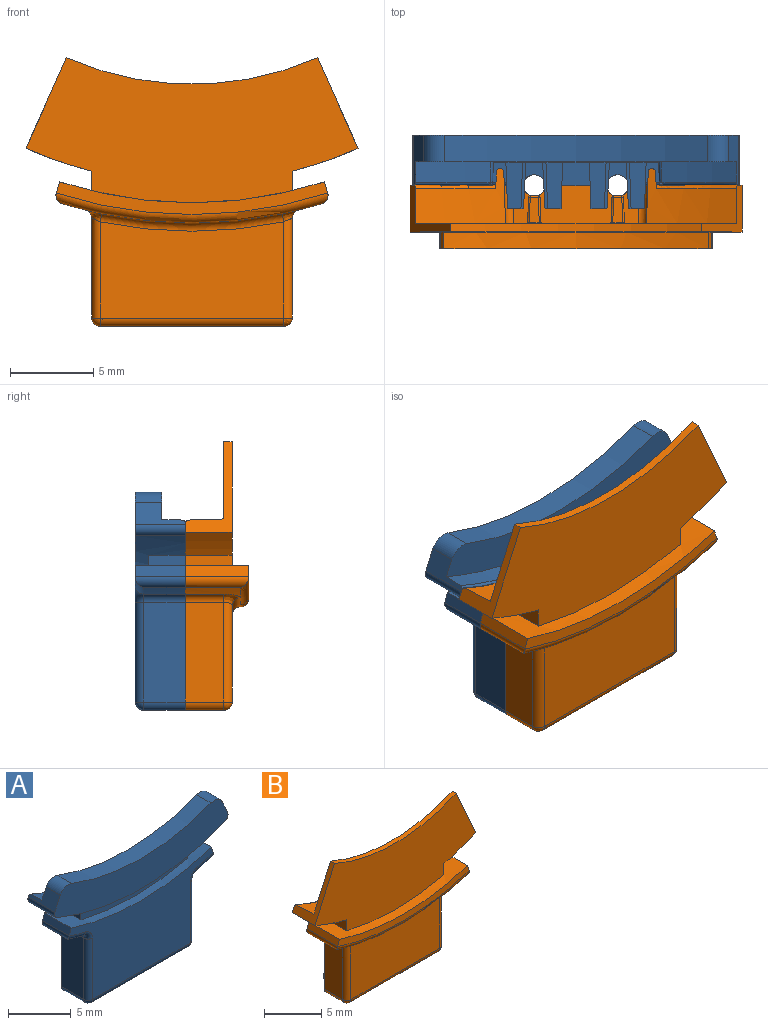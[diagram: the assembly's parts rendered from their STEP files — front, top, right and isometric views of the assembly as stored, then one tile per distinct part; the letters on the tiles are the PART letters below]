
ASSEMBLY  parts=2 mates=1
PART A: 159 faces, bbox 19.8x4.6x13.2 mm
  f0: cylinder r=0.47mm len=1.8mm, axis (0,1,0), area 5.4mm2, adj f12,f54
  f1: cylinder r=0.47mm len=1.8mm, axis (0,1,0), area 5.4mm2, adj f9,f53
  f2: cylinder r=25.6mm len=15.82mm, axis (0,-1,0), area 21.6mm2, adj f9,f12,f17,f21,f22,f26,f27,f31
  f3: cylinder r=24.45mm len=18.95mm, axis (0,-1,0), area 31.7mm2, adj f9,f12,f18,f22,f23,f25,f26,f31
  f4: cylinder r=21.5mm len=15.73mm, axis (0,-1,0), area 25.8mm2, adj f5,f14,f15,f18
  f5: plane 19.2x12.01mm, normal (0,1,0), area 97.3mm2, adj f4,f6,f7,f10,f11,f13,f14,f15
  f6: plane 1.68x1.59mm, normal (0,0.03,1), area 1.4mm2, adj f5,f8,f9,f37,f104,f144
  f7: plane 1.7x1.4mm, normal (0,0.03,1), area 2.3mm2, adj f5,f8,f99,f145
  f8: plane 3.7x1mm, normal (0,1,0), area 3.6mm2, adj f6,f7,f11,f30,f36,f37,f78,f79
  f9: plane 11.24x6.65mm, normal (0,1,0), area 15.3mm2, adj f1,f2,f3,f6,f16,f25,f26,f27
  f10: plane 1.21x0.84mm, normal (0,0.03,1), area 1mm2, adj f5,f35,f102,f153
  f11: plane 1.68x1.59mm, normal (0,0.03,1), area 1.4mm2, adj f5,f8,f12,f36,f57,f79
  f12: plane 11.24x6.65mm, normal (0,1,0), area 15.3mm2, adj f0,f2,f3,f11,f19,f20,f21,f22
  f13: plane 1.21x0.84mm, normal (0,0.03,1), area 1mm2, adj f5,f34,f56,f158
  f14: cylinder r=1mm len=1.6mm, axis (0,-1,0), area 2.4mm2, adj f4,f5,f18,f24
  f15: cylinder r=1mm len=1.6mm, axis (0,-1,0), area 2.4mm2, adj f4,f5,f16,f18
  f16: plane 3x1.34mm, normal (0.91,0,0.41), area 2.8mm2, adj f5,f9,f15,f18,f25,f33,f149
  f17: plane 16.25x8.15mm, normal (0,-1,0), area 82mm2, adj f2,f21,f27,f38,f40,f41,f43,f46
  f18: plane 19.57x4.51mm, normal (0,-1,0), area 56.3mm2, adj f3,f4,f14,f15,f16,f23,f24,f25
  f19: plane 5.99x2.5mm, normal (-1,0,0), area 15mm2, adj f12,f39,f42,f43
  f20: cylinder r=26.8mm len=2.5mm, axis (0,-1,0), area 3.7mm2, adj f12,f38,f39,f40
  f21: plane 3x0.66mm, normal (-0.95,0,0.31), area 2.1mm2, adj f2,f12,f17,f38
  f22: plane 2.2x1.18mm, normal (-1,0,0), area 2.6mm2, adj f2,f3,f12,f31
  f23: cylinder r=0.5mm len=3mm, axis (0,-1,0), area 2.4mm2, adj f3,f12,f18,f24
  f24: plane 3x1.34mm, normal (-0.91,0,0.41), area 2.8mm2, adj f5,f12,f14,f18,f23,f32,f155
  f25: cylinder r=0.5mm len=3mm, axis (0,-1,0), area 2.4mm2, adj f3,f9,f16,f18
  f26: plane 2.2x1.18mm, normal (1,0,0), area 2.6mm2, adj f2,f3,f9,f31
  f27: plane 3x0.66mm, normal (0.95,0,0.31), area 2.1mm2, adj f2,f9,f17,f50
  f28: cylinder r=26.8mm len=2.5mm, axis (0,-1,0), area 3.7mm2, adj f9,f48,f50,f52
  f29: plane 5.99x2.5mm, normal (1,0,0), area 15mm2, adj f9,f45,f48,f49
  f30: plane 11x2.5mm, normal (0,0,-1), area 26.2mm2, adj f8,f9,f12,f36,f37,f42,f45,f46
  f31: plane 12x1.9mm, normal (0,-1,0), area 13.9mm2, adj f2,f3,f22,f26
  f32: cone r=23.65mm half-angle=2deg, axis (0,1,0), area 5.7mm2, adj f5,f24,f154,f155
  f33: cone r=23.65mm half-angle=2deg, axis (0,1,0), area 5.7mm2, adj f5,f16,f149,f150
  f34: plane 7.56x1.21mm, normal (1,0.03,0), area 9.1mm2, adj f5,f13,f154,f157
  f35: plane 7.56x1.21mm, normal (-1,0.03,0), area 9.1mm2, adj f5,f10,f150,f152
  f36: cylinder r=0.65mm len=1.3mm, axis (0,0,-1), area 2mm2, adj f8,f11,f12,f30
  f37: cylinder r=0.65mm len=1.3mm, axis (0,0,-1), area 2mm2, adj f6,f8,f9,f30
  f38: cylinder r=0.5mm len=3mm, axis (0,-1,0), area 2.2mm2, adj f12,f17,f20,f21,f40
  f39: cylinder r=0.5mm len=2.5mm, axis (0,-1,0), area 1.7mm2, adj f12,f19,f20,f41
  f40: torus R=26.3mm, axis (0,-1,0), area 1.3mm2, adj f17,f20,f38,f41
  f41: torus R=1mm, axis (0,-1,0), area 0.7mm2, adj f17,f39,f40,f43
  f42: cylinder r=0.5mm len=2.5mm, axis (0,-1,0), area 2mm2, adj f12,f19,f30,f44
  f43: cylinder r=0.5mm len=5.99mm, axis (0,0,-1), area 4.7mm2, adj f17,f19,f41,f44
  f44: sphere r=0.5mm, area 0.5mm2, adj f42,f43,f46
  f45: cylinder r=0.5mm len=2.5mm, axis (0,-1,0), area 2mm2, adj f9,f29,f30,f47
  f46: cylinder r=0.5mm len=11mm, axis (1,0,0), area 8.6mm2, adj f17,f30,f44,f47
  f47: sphere r=0.5mm, area 0.2mm2, adj f45,f46,f49
  f48: cylinder r=0.5mm len=2.5mm, axis (0,-1,0), area 1.7mm2, adj f9,f28,f29,f51
  f49: cylinder r=0.5mm len=5.99mm, axis (0,0,1), area 4.7mm2, adj f17,f29,f47,f51
  f50: cylinder r=0.5mm len=3mm, axis (0,-1,0), area 2.2mm2, adj f9,f17,f27,f28,f52
  f51: torus R=1mm, axis (0,-1,0), area 0.7mm2, adj f17,f48,f49,f52
  f52: torus R=26.3mm, axis (0,-1,0), area 1.3mm2, adj f17,f28,f50,f51
  f53: plane 0.95x0.95mm, normal (0,1,0), area 0.7mm2, adj f1
  f54: plane 0.95x0.95mm, normal (0,1,0), area 0.7mm2, adj f0
  f55: plane 1.4x0.4mm, normal (0,0.03,-1), area 0.5mm2, adj f12,f57,f77,f148
  f56: plane 5.46x2.81mm, normal (-1,0.03,0), area 14mm2, adj f5,f12,f13,f58,f77,f148,f158
  f57: plane 2.8x0.47mm, normal (1,0.03,0), area 1.2mm2, adj f5,f11,f12,f55,f76,f77
  f58: plane 2.8x1mm, normal (0,0.03,1), area 2.5mm2, adj f5,f56,f59,f77
  f59: plane 2.8x0.6mm, normal (1,0.03,0), area 1.4mm2, adj f5,f58,f60,f77
  f60: plane 2.8x0.3mm, normal (0,0.03,1), area 0.5mm2, adj f5,f59,f61,f77
  f61: plane 2.8x0.5mm, normal (0.93,0.03,-0.37), area 1.3mm2, adj f5,f60,f62,f77
  f62: plane 2.8x0.52mm, normal (1,0.03,0), area 1.3mm2, adj f5,f61,f63,f77
  f63: plane 2.8x0.3mm, normal (0,0.03,1), area 0.5mm2, adj f5,f62,f64,f77
  f64: plane 2.8x0.5mm, normal (0.93,0.03,-0.37), area 1.3mm2, adj f5,f63,f65,f77
  f65: plane 2.8x0.52mm, normal (1,0.03,0), area 1.3mm2, adj f5,f64,f66,f77
  f66: plane 2.8x0.3mm, normal (0,0.03,1), area 0.5mm2, adj f5,f65,f67,f77
  f67: plane 2.8x0.5mm, normal (0.93,0.03,-0.37), area 1.3mm2, adj f5,f66,f68,f77
  f68: plane 2.8x0.52mm, normal (1,0.03,0), area 1.3mm2, adj f5,f67,f69,f77
  f69: plane 2.8x0.3mm, normal (0,0.03,1), area 0.5mm2, adj f5,f68,f70,f77
  f70: plane 2.8x0.5mm, normal (0.93,0.03,-0.37), area 1.3mm2, adj f5,f69,f71,f77
  f71: plane 2.8x0.52mm, normal (1,0.03,0), area 1.3mm2, adj f5,f70,f72,f77
  f72: plane 2.8x0.3mm, normal (0,0.03,1), area 0.5mm2, adj f5,f71,f73,f77
  f73: plane 2.8x0.5mm, normal (0.93,0.03,-0.37), area 1.3mm2, adj f5,f72,f74,f77
  f74: plane 2.8x0.52mm, normal (1,0.03,0), area 1.3mm2, adj f5,f73,f75,f77
  f75: plane 2.8x0.3mm, normal (0,0.03,1), area 0.5mm2, adj f5,f74,f76,f77
  f76: plane 2.8x0.5mm, normal (0.93,0.03,-0.37), area 1.3mm2, adj f5,f57,f75,f77
  f77: plane 5.82x0.98mm, normal (0,1,0), area 4.8mm2, adj f55,f56,f57,f58,f59,f60,f61,f62
  f78: plane 1.4x0.9mm, normal (0,0.03,-1), area 1.2mm2, adj f8,f79,f99,f100
  f79: plane 2.8x0.47mm, normal (-1,0.03,0), area 1.2mm2, adj f5,f8,f11,f78,f80,f100
  f80: plane 2.8x0.5mm, normal (-0.93,0.03,-0.37), area 1.3mm2, adj f5,f79,f81,f100
  f81: plane 2.8x0.3mm, normal (0,0.03,1), area 0.5mm2, adj f5,f80,f82,f100
  f82: plane 2.8x0.52mm, normal (-1,0.03,0), area 1.3mm2, adj f5,f81,f83,f100
  f83: plane 2.8x0.5mm, normal (-0.93,0.03,-0.37), area 1.3mm2, adj f5,f82,f84,f100
  f84: plane 2.8x0.3mm, normal (0,0.03,1), area 0.5mm2, adj f5,f83,f85,f100
  f85: plane 2.8x0.52mm, normal (-1,0.03,0), area 1.3mm2, adj f5,f84,f86,f100
  f86: plane 2.8x0.5mm, normal (-0.93,0.03,-0.37), area 1.3mm2, adj f5,f85,f87,f100
  f87: plane 2.8x0.3mm, normal (0,0.03,1), area 0.5mm2, adj f5,f86,f88,f100
  f88: plane 2.8x0.52mm, normal (-1,0.03,0), area 1.3mm2, adj f5,f87,f89,f100
  f89: plane 2.8x0.5mm, normal (-0.93,0.03,-0.37), area 1.3mm2, adj f5,f88,f90,f100
  f90: plane 2.8x0.3mm, normal (0,0.03,1), area 0.5mm2, adj f5,f89,f91,f100
  f91: plane 2.8x0.52mm, normal (-1,0.03,0), area 1.3mm2, adj f5,f90,f92,f100
  f92: plane 2.8x0.5mm, normal (-0.93,0.03,-0.37), area 1.3mm2, adj f5,f91,f93,f100
  f93: plane 2.8x0.3mm, normal (0,0.03,1), area 0.5mm2, adj f5,f92,f94,f100
  f94: plane 2.8x0.52mm, normal (-1,0.03,0), area 1.3mm2, adj f5,f93,f95,f100
  f95: plane 2.8x0.5mm, normal (-0.93,0.03,-0.37), area 1.3mm2, adj f5,f94,f96,f100
  f96: plane 2.8x0.3mm, normal (0,0.03,1), area 0.5mm2, adj f5,f95,f97,f100
  f97: plane 2.8x0.6mm, normal (-1,0.03,0), area 1.4mm2, adj f5,f96,f98,f100
  f98: plane 2.8x1mm, normal (0,0.03,1), area 2.5mm2, adj f5,f97,f99,f100
  f99: plane 5.95x2.8mm, normal (1,0.03,0), area 16.4mm2, adj f5,f7,f8,f78,f98,f100
  f100: plane 5.8x0.96mm, normal (0,1,0), area 4.8mm2, adj f78,f79,f80,f81,f82,f83,f84,f85
  f101: plane 1.4x0.4mm, normal (0,0.03,-1), area 0.5mm2, adj f9,f104,f123,f147
  f102: plane 5.46x2.81mm, normal (1,0.03,0), area 14mm2, adj f5,f9,f10,f103,f123,f147,f153
  f103: plane 2.8x1mm, normal (0,0.03,1), area 2.5mm2, adj f5,f102,f122,f123
  f104: plane 2.8x0.47mm, normal (-1,0.03,0), area 1.2mm2, adj f5,f6,f9,f101,f105,f123
  f105: plane 2.8x0.5mm, normal (-0.93,0.03,-0.37), area 1.3mm2, adj f5,f104,f106,f123
  f106: plane 2.8x0.3mm, normal (0,0.03,1), area 0.5mm2, adj f5,f105,f107,f123
  f107: plane 2.8x0.52mm, normal (-1,0.03,0), area 1.3mm2, adj f5,f106,f108,f123
  f108: plane 2.8x0.5mm, normal (-0.93,0.03,-0.37), area 1.3mm2, adj f5,f107,f109,f123
  f109: plane 2.8x0.3mm, normal (0,0.03,1), area 0.5mm2, adj f5,f108,f110,f123
  f110: plane 2.8x0.52mm, normal (-1,0.03,0), area 1.3mm2, adj f5,f109,f111,f123
  f111: plane 2.8x0.5mm, normal (-0.93,0.03,-0.37), area 1.3mm2, adj f5,f110,f112,f123
  f112: plane 2.8x0.3mm, normal (0,0.03,1), area 0.5mm2, adj f5,f111,f113,f123
  f113: plane 2.8x0.52mm, normal (-1,0.03,0), area 1.3mm2, adj f5,f112,f114,f123
  f114: plane 2.8x0.5mm, normal (-0.93,0.03,-0.37), area 1.3mm2, adj f5,f113,f115,f123
  f115: plane 2.8x0.3mm, normal (0,0.03,1), area 0.5mm2, adj f5,f114,f116,f123
  f116: plane 2.8x0.52mm, normal (-1,0.03,0), area 1.3mm2, adj f5,f115,f117,f123
  f117: plane 2.8x0.5mm, normal (-0.93,0.03,-0.37), area 1.3mm2, adj f5,f116,f118,f123
  f118: plane 2.8x0.3mm, normal (0,0.03,1), area 0.5mm2, adj f5,f117,f119,f123
  f119: plane 2.8x0.52mm, normal (-1,0.03,0), area 1.3mm2, adj f5,f118,f120,f123
  f120: plane 2.8x0.5mm, normal (-0.93,0.03,-0.37), area 1.3mm2, adj f5,f119,f121,f123
  f121: plane 2.8x0.3mm, normal (0,0.03,1), area 0.5mm2, adj f5,f120,f122,f123
  f122: plane 2.8x0.6mm, normal (-1,0.03,0), area 1.4mm2, adj f5,f103,f121,f123
  f123: plane 5.82x0.98mm, normal (0,1,0), area 4.8mm2, adj f101,f102,f103,f104,f105,f106,f107,f108
  f124: plane 1.4x0.9mm, normal (0,0.03,-1), area 1.2mm2, adj f8,f144,f145,f146
  f125: plane 2.8x1mm, normal (0,0.03,1), area 2.5mm2, adj f5,f126,f145,f146
  f126: plane 2.8x0.6mm, normal (1,0.03,0), area 1.4mm2, adj f5,f125,f127,f146
  f127: plane 2.8x0.3mm, normal (0,0.03,1), area 0.5mm2, adj f5,f126,f128,f146
  f128: plane 2.8x0.5mm, normal (0.93,0.03,-0.37), area 1.3mm2, adj f5,f127,f129,f146
  f129: plane 2.8x0.52mm, normal (1,0.03,0), area 1.3mm2, adj f5,f128,f130,f146
  f130: plane 2.8x0.3mm, normal (0,0.03,1), area 0.5mm2, adj f5,f129,f131,f146
  f131: plane 2.8x0.5mm, normal (0.93,0.03,-0.37), area 1.3mm2, adj f5,f130,f132,f146
  f132: plane 2.8x0.52mm, normal (1,0.03,0), area 1.3mm2, adj f5,f131,f133,f146
  f133: plane 2.8x0.3mm, normal (0,0.03,1), area 0.5mm2, adj f5,f132,f134,f146
  f134: plane 2.8x0.5mm, normal (0.93,0.03,-0.37), area 1.3mm2, adj f5,f133,f135,f146
  f135: plane 2.8x0.52mm, normal (1,0.03,0), area 1.3mm2, adj f5,f134,f136,f146
  f136: plane 2.8x0.3mm, normal (0,0.03,1), area 0.5mm2, adj f5,f135,f137,f146
  f137: plane 2.8x0.5mm, normal (0.93,0.03,-0.37), area 1.3mm2, adj f5,f136,f138,f146
  f138: plane 2.8x0.52mm, normal (1,0.03,0), area 1.3mm2, adj f5,f137,f139,f146
  f139: plane 2.8x0.3mm, normal (0,0.03,1), area 0.5mm2, adj f5,f138,f140,f146
  f140: plane 2.8x0.5mm, normal (0.93,0.03,-0.37), area 1.3mm2, adj f5,f139,f141,f146
  f141: plane 2.8x0.52mm, normal (1,0.03,0), area 1.3mm2, adj f5,f140,f142,f146
  f142: plane 2.8x0.3mm, normal (0,0.03,1), area 0.5mm2, adj f5,f141,f143,f146
  f143: plane 2.8x0.5mm, normal (0.93,0.03,-0.37), area 1.3mm2, adj f5,f142,f144,f146
  f144: plane 2.8x0.47mm, normal (1,0.03,0), area 1.2mm2, adj f5,f6,f8,f124,f143,f146
  f145: plane 5.95x2.8mm, normal (-1,0.03,0), area 16.4mm2, adj f5,f7,f8,f124,f125,f146
  f146: plane 5.8x0.96mm, normal (0,1,0), area 4.8mm2, adj f124,f125,f126,f127,f128,f129,f130,f131
  f147: cylinder r=0.5mm len=1.41mm, axis (0.03,-1,-0.03), area 1.1mm2, adj f9,f101,f102,f123
  f148: cylinder r=0.5mm len=1.41mm, axis (-0.03,-1,-0.03), area 1.1mm2, adj f12,f55,f56,f77
  f149: torus R=23.84mm, axis (0,-1,0), area 1.5mm2, adj f9,f16,f33,f151
  f150: cylinder r=0.2mm len=1.21mm, axis (0.03,1,-0.03), area 0.3mm2, adj f5,f33,f35,f151
  f151: sphere r=0.2mm, area 0mm2, adj f149,f150,f152
  f152: cylinder r=0.2mm len=7.72mm, axis (0,0,-1), area 2.3mm2, adj f9,f35,f151,f153
  f153: cylinder r=0.2mm len=1.04mm, axis (-1,0,0), area 0.3mm2, adj f9,f10,f102,f152
  f154: cylinder r=0.2mm len=1.21mm, axis (-0.03,1,-0.03), area 0.3mm2, adj f5,f32,f34,f156
  f155: torus R=23.84mm, axis (0,-1,0), area 1.5mm2, adj f12,f24,f32,f156
  f156: sphere r=0.2mm, area 0mm2, adj f154,f155,f157
  f157: cylinder r=0.2mm len=7.72mm, axis (0,0,-1), area 2.3mm2, adj f12,f34,f156,f158
  f158: cylinder r=0.2mm len=1.04mm, axis (1,0,0), area 0.3mm2, adj f12,f13,f56,f157
PART B: 122 faces, bbox 20.1x5x16.3 mm
  f0: bspline ~0.14x0.13mm, area 0mm2, adj f16,f115,f118,f119
  f1: bspline ~0.14x0.13mm, area 0mm2, adj f16,f113,f114,f117
  f2: bspline ~0.14x0.13mm, area 0mm2, adj f16,f107,f112,f116
  f3: bspline ~0.14x0.13mm, area 0mm2, adj f16,f103,f108,f109
  f4: bspline ~0.14x0.13mm, area 0mm2, adj f16,f95,f98,f99
  f5: bspline ~0.14x0.13mm, area 0mm2, adj f16,f93,f94,f97
  f6: bspline ~0.14x0.13mm, area 0mm2, adj f16,f87,f92,f96
  f7: bspline ~0.14x0.13mm, area 0mm2, adj f16,f83,f88,f89
  f8: cone r=0.27mm half-angle=45deg, axis (0,-1,0), area 0.3mm2, adj f11,f68
  f9: cone r=0.27mm half-angle=45deg, axis (0,-1,0), area 0.3mm2, adj f10,f69
  f10: cone r=0.4mm half-angle=2deg, axis (0,-1,0), area 1.9mm2, adj f9,f18
  f11: cone r=0.4mm half-angle=2deg, axis (0,-1,0), area 1.9mm2, adj f8,f21
  f12: torus R=27.3mm, axis (0,-1,0), area 8.6mm2, adj f13,f36,f58,f60
  f13: torus R=26.3mm, axis (0,-1,0), area 12.7mm2, adj f12,f17,f33,f42,f55,f56
  f14: cylinder r=25.6mm len=15.82mm, axis (0,-1,0), area 27.2mm2, adj f18,f19,f21,f25,f26,f31,f32,f42
  f15: cylinder r=18.5mm len=15.05mm, axis (0,-1,0), area 7.7mm2, adj f16,f19,f28,f29
  f16: plane 19.19x15.23mm, normal (0,1,0), area 156.2mm2, adj f0,f1,f2,f3,f4,f5,f6,f7
  f17: cylinder r=26.8mm len=3.3mm, axis (0,-1,0), area 5.3mm2, adj f13,f21,f56,f60,f61
  f18: plane 11.24x6.81mm, normal (0,1,0), area 18.5mm2, adj f10,f14,f22,f24,f25,f26,f27,f28
  f19: plane 19.89x8.7mm, normal (0,-1,0), area 121mm2, adj f14,f15,f26,f27,f28,f29,f30,f31
  f20: plane 3.7x0.8mm, normal (0,1,0), area 3mm2, adj f22,f23,f35,f39
  f21: plane 11.24x6.81mm, normal (0,1,0), area 18.5mm2, adj f11,f14,f17,f23,f29,f30,f31,f32
  f22: cylinder r=0.65mm len=1.3mm, axis (0,0,-1), area 1.6mm2, adj f18,f20,f35,f39
  f23: cylinder r=0.65mm len=1.3mm, axis (0,0,-1), area 1.6mm2, adj f20,f21,f35,f39
  f24: plane 5.99x2.3mm, normal (-1,0,0), area 13.8mm2, adj f18,f49,f53,f54
  f25: plane 3.8x0.66mm, normal (-0.95,0,0.31), area 2.6mm2, adj f14,f18,f42,f55
  f26: plane 2.8x1.18mm, normal (-1,0,0), area 3.3mm2, adj f14,f18,f19,f27
  f27: cylinder r=24.45mm len=3.94mm, axis (0,-1,0), area 11.7mm2, adj f18,f19,f26,f28
  f28: plane 5.44x2.8mm, normal (-0.91,0,0.41), area 4.9mm2, adj f15,f16,f18,f19,f27,f37,f63
  f29: plane 5.44x2.8mm, normal (0.91,0,0.41), area 4.9mm2, adj f15,f16,f19,f21,f30,f38,f62
  f30: cylinder r=24.45mm len=3.94mm, axis (0,-1,0), area 11.7mm2, adj f19,f21,f29,f31
  f31: plane 2.8x1.18mm, normal (1,0,0), area 3.3mm2, adj f14,f19,f21,f30
  f32: plane 3.8x0.66mm, normal (0.95,0,0.31), area 2.6mm2, adj f14,f21,f42,f56
  f33: cylinder r=26.8mm len=3.3mm, axis (0,-1,0), area 5.3mm2, adj f13,f18,f54,f55,f58
  f34: plane 5.99x2.3mm, normal (1,0,0), area 13.8mm2, adj f21,f51,f59,f61
  f35: plane 11x2.3mm, normal (0,0,-1), area 24mm2, adj f18,f20,f21,f22,f23,f49,f51,f52
  f36: plane 11x5.76mm, normal (0,-1,0), area 59.2mm2, adj f12,f52,f53,f59
  f37: cone r=23.65mm half-angle=2deg, axis (0,1,0), area 12.4mm2, adj f16,f28,f40,f44,f45,f63,f64,f67
  f38: cone r=23.65mm half-angle=2deg, axis (0,1,0), area 12.4mm2, adj f16,f29,f41,f46,f48,f62,f65,f66
  f39: plane 7.79x2.49mm, normal (0,0.03,1), area 16mm2, adj f16,f18,f20,f21,f22,f23,f120,f121
  f40: plane 8.51x3.11mm, normal (1,0.03,0), area 25.2mm2, adj f16,f18,f37,f43,f64,f120
  f41: plane 8.51x3.11mm, normal (-1,0.03,0), area 25.2mm2, adj f16,f21,f38,f47,f65,f121
  f42: plane 16.25x1.95mm, normal (0,-1,0), area 11.4mm2, adj f13,f14,f25,f32,f55,f56
  f43: plane 1.01x0.51mm, normal (0,0.03,-1), area 0.4mm2, adj f18,f40,f44,f45,f64,f67
  f44: plane 7.26x1.01mm, normal (-1,0.03,0), area 5.8mm2, adj f18,f37,f43,f63,f67
  f45: plane 7.12x0.04mm, normal (0,1,0), area 0.3mm2, adj f37,f43,f64,f67
  f46: plane 7.26x1.01mm, normal (1,0.03,0), area 5.8mm2, adj f21,f38,f47,f62,f66
  f47: plane 1.01x0.51mm, normal (0,0.03,-1), area 0.4mm2, adj f21,f41,f46,f48,f65,f66
  f48: plane 7.12x0.04mm, normal (0,1,0), area 0.3mm2, adj f38,f47,f65,f66
  f49: cylinder r=0.5mm len=2.3mm, axis (0,-1,0), area 1.8mm2, adj f18,f24,f35,f50
  f50: sphere r=0.5mm, area 0.5mm2, adj f49,f52,f53
  f51: cylinder r=0.5mm len=2.3mm, axis (0,-1,0), area 1.8mm2, adj f21,f34,f35,f57
  f52: cylinder r=0.5mm len=11mm, axis (1,0,0), area 8.6mm2, adj f35,f36,f50,f57
  f53: cylinder r=0.5mm len=5.99mm, axis (0,0,-1), area 4.6mm2, adj f24,f36,f50,f58
  f54: cylinder r=0.5mm len=2.3mm, axis (0,-1,0), area 1.5mm2, adj f18,f24,f33,f58
  f55: cylinder r=0.5mm len=3.8mm, axis (0,-1,0), area 2.9mm2, adj f13,f18,f25,f33,f42
  f56: cylinder r=0.5mm len=3.8mm, axis (0,-1,0), area 2.9mm2, adj f13,f17,f21,f32,f42
  f57: sphere r=0.5mm, area 0.2mm2, adj f51,f52,f59
  f58: bspline ~1x0.98mm, area 0.8mm2, adj f12,f33,f53,f54
  f59: cylinder r=0.5mm len=5.99mm, axis (0,0,1), area 4.6mm2, adj f34,f36,f57,f60
  f60: bspline ~1x0.98mm, area 0.8mm2, adj f12,f17,f59,f61
  f61: cylinder r=0.5mm len=2.3mm, axis (0,-1,0), area 1.5mm2, adj f17,f21,f34,f60
  f62: torus R=23.84mm, axis (0,-1,0), area 1.6mm2, adj f21,f29,f38,f46
  f63: torus R=23.84mm, axis (0,-1,0), area 1.6mm2, adj f18,f28,f37,f44
  f64: cylinder r=0.2mm len=7.12mm, axis (0,0,1), area 2.2mm2, adj f37,f40,f43,f45
  f65: cylinder r=0.2mm len=7.12mm, axis (0,0,-1), area 2.2mm2, adj f38,f41,f47,f48
  f66: cylinder r=0.2mm len=7.18mm, axis (0,0,1), area 2.2mm2, adj f38,f46,f47,f48
  f67: cylinder r=0.2mm len=7.18mm, axis (0,0,1), area 2.2mm2, adj f37,f43,f44,f45
  f68: plane 0.54x0.54mm, normal (0,1,0), area 0.2mm2, adj f8
  f69: plane 0.54x0.54mm, normal (0,1,0), area 0.2mm2, adj f9
  f70: plane 2.79x1.51mm, normal (-1,0.03,0), area 4.1mm2, adj f80,f83,f87,f88
  f71: plane 1.51x0.59mm, normal (0,0.03,1), area 0.8mm2, adj f83,f84,f93,f94
  f72: plane 2.79x1.51mm, normal (1,0.03,0), area 4.1mm2, adj f85,f94,f95,f99
  f73: plane 1.51x0.59mm, normal (0,0.03,-1), area 0.8mm2, adj f86,f87,f95,f96
  f74: plane 2.69x0.49mm, normal (0,1,0), area 1.3mm2, adj f80,f84,f85,f86
  f75: plane 2.79x1.51mm, normal (-1,0.03,0), area 4.1mm2, adj f103,f104,f113,f114
  f76: plane 1.51x0.59mm, normal (0,0.03,1), area 0.8mm2, adj f105,f114,f115,f119
  f77: plane 2.79x1.51mm, normal (1,0.03,0), area 4.1mm2, adj f106,f107,f115,f116
  f78: plane 1.51x0.59mm, normal (0,0.03,-1), area 0.8mm2, adj f100,f103,f107,f108
  f79: plane 2.69x0.49mm, normal (0,1,0), area 1.3mm2, adj f100,f104,f105,f106
  f80: cylinder r=0.1mm len=2.69mm, axis (0,0,1), area 0.4mm2, adj f70,f74,f81,f82
  f81: sphere r=0.1mm, area 0mm2, adj f80,f83,f84
  f82: sphere r=0.1mm, area 0mm2, adj f80,f86,f87
  f83: cylinder r=0.1mm len=1.51mm, axis (-0.03,-1,0.03), area 0.2mm2, adj f7,f70,f71,f81,f89
  f84: cylinder r=0.1mm len=0.49mm, axis (1,0,0), area 0.1mm2, adj f71,f74,f81,f90
  f85: cylinder r=0.1mm len=2.69mm, axis (0,0,-1), area 0.4mm2, adj f72,f74,f90,f91
  f86: cylinder r=0.1mm len=0.49mm, axis (-1,0,0), area 0.1mm2, adj f73,f74,f82,f91
  f87: cylinder r=0.1mm len=1.51mm, axis (-0.03,-1,-0.03), area 0.2mm2, adj f6,f70,f73,f82,f92
  f88: cylinder r=0.1mm len=2.79mm, axis (0,0,1), area 0.4mm2, adj f7,f16,f70,f92
  f89: bspline ~0.14x0.13mm, area 0mm2, adj f7,f16,f83,f93
  f90: sphere r=0.1mm, area 0mm2, adj f84,f85,f94
  f91: sphere r=0.1mm, area 0mm2, adj f85,f86,f95
  f92: bspline ~0.14x0.13mm, area 0mm2, adj f6,f16,f87,f88
  f93: cylinder r=0.1mm len=0.59mm, axis (1,0,0), area 0.1mm2, adj f5,f16,f71,f89
  f94: cylinder r=0.1mm len=1.51mm, axis (0.03,-1,0.03), area 0.2mm2, adj f5,f71,f72,f90,f97
  f95: cylinder r=0.1mm len=1.51mm, axis (0.03,-1,-0.03), area 0.2mm2, adj f4,f72,f73,f91,f98
  f96: cylinder r=0.1mm len=0.59mm, axis (-1,0,0), area 0.1mm2, adj f6,f16,f73,f98
  f97: bspline ~0.14x0.13mm, area 0mm2, adj f5,f16,f94,f99
  f98: bspline ~0.14x0.13mm, area 0mm2, adj f4,f16,f95,f96
  f99: cylinder r=0.1mm len=2.79mm, axis (0,0,-1), area 0.4mm2, adj f4,f16,f72,f97
  f100: cylinder r=0.1mm len=0.49mm, axis (1,0,0), area 0.1mm2, adj f78,f79,f101,f102
  f101: sphere r=0.1mm, area 0mm2, adj f100,f103,f104
  f102: sphere r=0.1mm, area 0mm2, adj f100,f106,f107
  f103: cylinder r=0.1mm len=1.51mm, axis (-0.03,-1,-0.03), area 0.2mm2, adj f3,f75,f78,f101,f109
  f104: cylinder r=0.1mm len=2.69mm, axis (0,0,-1), area 0.4mm2, adj f75,f79,f101,f110
  f105: cylinder r=0.1mm len=0.49mm, axis (-1,0,0), area 0.1mm2, adj f76,f79,f110,f111
  f106: cylinder r=0.1mm len=2.69mm, axis (0,0,1), area 0.4mm2, adj f77,f79,f102,f111
  f107: cylinder r=0.1mm len=1.51mm, axis (0.03,-1,-0.03), area 0.2mm2, adj f2,f77,f78,f102,f112
  f108: cylinder r=0.1mm len=0.59mm, axis (-1,0,0), area 0.1mm2, adj f3,f16,f78,f112
  f109: bspline ~0.14x0.13mm, area 0mm2, adj f3,f16,f103,f113
  f110: sphere r=0.1mm, area 0mm2, adj f104,f105,f114
  f111: sphere r=0.1mm, area 0mm2, adj f105,f106,f115
  f112: bspline ~0.14x0.13mm, area 0mm2, adj f2,f16,f107,f108
  f113: cylinder r=0.1mm len=2.79mm, axis (0,0,1), area 0.4mm2, adj f1,f16,f75,f109
  f114: cylinder r=0.1mm len=1.51mm, axis (-0.03,-1,0.03), area 0.2mm2, adj f1,f75,f76,f110,f117
  f115: cylinder r=0.1mm len=1.51mm, axis (0.03,-1,0.03), area 0.2mm2, adj f0,f76,f77,f111,f118
  f116: cylinder r=0.1mm len=2.79mm, axis (0,0,-1), area 0.4mm2, adj f2,f16,f77,f118
  f117: bspline ~0.14x0.13mm, area 0mm2, adj f1,f16,f114,f119
  f118: bspline ~0.14x0.13mm, area 0mm2, adj f0,f16,f115,f116
  f119: cylinder r=0.1mm len=0.59mm, axis (1,0,0), area 0.1mm2, adj f0,f16,f76,f117
  f120: cylinder r=0.5mm len=2.31mm, axis (0.03,-1,0.03), area 1.8mm2, adj f16,f18,f39,f40
  f121: cylinder r=0.5mm len=2.31mm, axis (-0.03,-1,0.03), area 1.8mm2, adj f16,f21,f39,f41
PLACE A rot(axis=(0,0,1),180deg) t=(16.11,5.26,12.29)mm
PLACE B t=(16.11,-0.54,12.29)mm
MATE fastened A.f1 <-> B.f9  axis (0,-1,0) through (11.16,2.26,-19.66)mm
